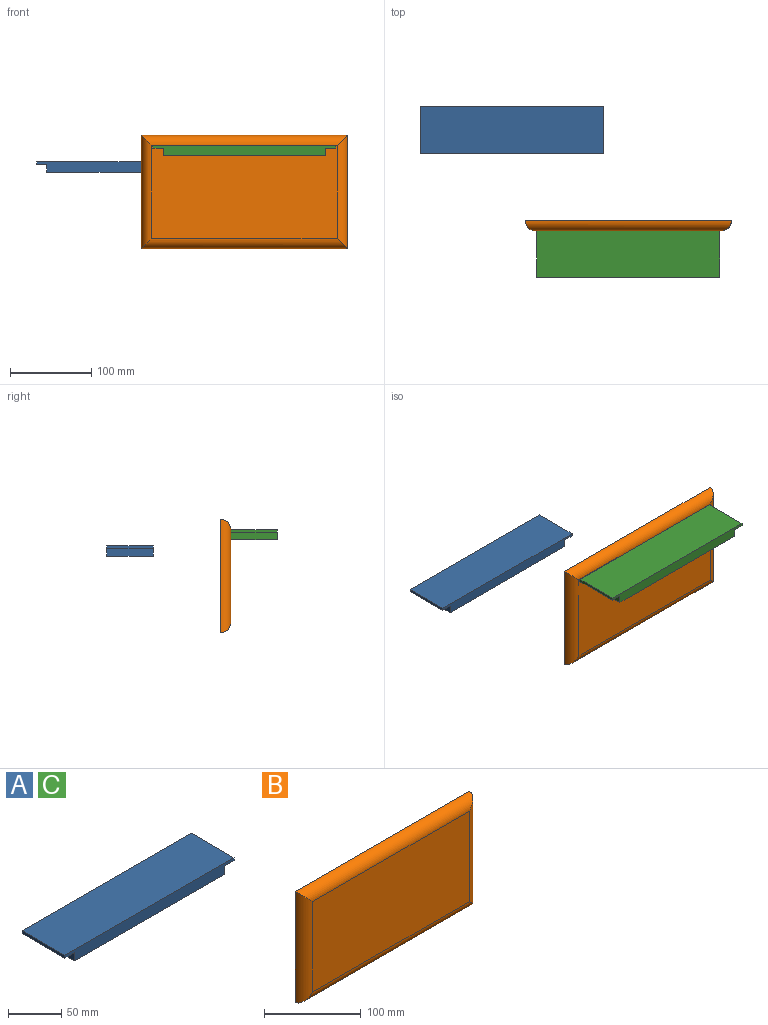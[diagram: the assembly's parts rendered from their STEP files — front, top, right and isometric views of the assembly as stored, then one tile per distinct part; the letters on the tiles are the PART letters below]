
ASSEMBLY  parts=3 mates=1
PART A: 10 faces, bbox 225.4x57.2x12.7 mm
  f0: plane 225.43x57.15mm, normal (0,0,1), area 12883mm2, adj f1,f7,f8,f9
  f1: plane 57.15x3.18mm, normal (-1,0,0), area 181.5mm2, adj f0,f2,f8,f9
  f2: plane 57.15x12.7mm, normal (0,0,-1), area 725.8mm2, adj f1,f3,f8,f9
  f3: plane 57.15x9.53mm, normal (-1,0,0), area 544.4mm2, adj f2,f4,f8,f9
  f4: plane 200.03x57.15mm, normal (0,0,-1), area 11431.4mm2, adj f3,f5,f8,f9
  f5: plane 57.15x9.53mm, normal (1,0,0), area 544.4mm2, adj f4,f6,f8,f9
  f6: plane 57.15x12.7mm, normal (0,0,-1), area 725.8mm2, adj f5,f7,f8,f9
  f7: plane 57.15x3.18mm, normal (1,0,0), area 181.5mm2, adj f0,f6,f8,f9
  f8: plane 225.43x12.7mm, normal (0,-1,0), area 2621mm2, adj f0,f1,f2,f3,f4,f5,f6,f7
  f9: plane 225.43x12.7mm, normal (0,1,0), area 2621mm2, adj f0,f1,f2,f3,f4,f5,f6,f7
PART B: 6 faces, bbox 254x12.7x139.7 mm
  f0: plane 228.6x114.3mm, normal (0,-1,0), area 26129mm2, adj f2,f3,f4,f5
  f1: plane 254x139.7mm, normal (0,1,0), area 35483.8mm2, adj f2,f3,f4,f5
  f2: cylinder r=12.7mm len=254mm, axis (1,0,0), area 4882.9mm2, adj f0,f1,f3,f4
  f3: cylinder r=12.7mm len=139.7mm, axis (0,0,1), area 2602.8mm2, adj f0,f1,f2,f5
  f4: cylinder r=12.7mm len=139.7mm, axis (0,0,-1), area 2602.8mm2, adj f0,f1,f2,f5
  f5: cylinder r=12.7mm len=254mm, axis (-1,0,0), area 4882.9mm2, adj f0,f1,f3,f4
PART C: same geometry as A
PLACE A t=(-133.25,146.47,37.09)mm
PLACE B t=(87.1,6.35,-7.86)mm
PLACE C t=(10.13,-6.35,57.15)mm
MATE planar C.f9 <-> B.f0  axis (0,1,0) through (0,-6.35,57.15)mm
